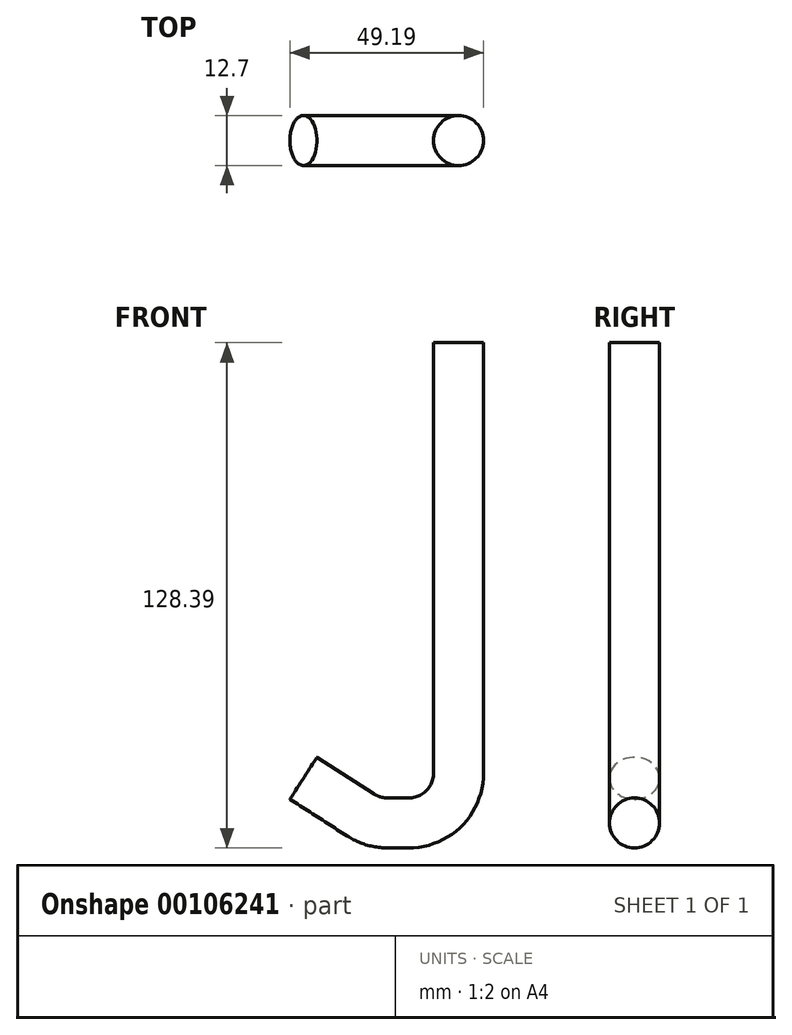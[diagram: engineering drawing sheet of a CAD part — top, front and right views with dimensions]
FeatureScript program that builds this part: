
annotation { "Feature Type Name" : "Feature", "Feature Type Description" : "" }
export const myFeature = defineFeature(function(context is Context, id is Id, definition is map)
    precondition{}
    {
        {
            var Q0;
            Q0=qCreatedBy(makeId("Front.planeOp"),FACE);
            var sketch = newSketch(context, id + "F0", { "sketchPlane" : qUnion([Q0])});
            skLineSegment(sketch, "E0", {"start": v(0, 63.86) * mm, "end": v(0, -45.48) * mm});
            skLineSegment(sketch, "E1", {"start": v(-12.7, -58.18) * mm, "end": v(-18, -58.18) * mm});
            skLineSegment(sketch, "E2", {"start": v(-24.86, -56.17) * mm, "end": v(-39.4, -46.83) * mm});
            skPoint(sketch, "E3.visualSharp", {"position": v(0, -58.18) * mm});
            skArc(sketch, "E3.filletArc", {"start": v(-12.7, -58.18) * mm, "mid": v(-3.72, -54.46) * mm, "end": v(0, -45.48) * mm});
            skPoint(sketch, "E4.visualSharp", {"position": v(-21.72, -58.18) * mm});
            skArc(sketch, "E4.filletArc", {"start": v(-24.86, -56.17) * mm, "mid": v(-21.57, -57.67) * mm, "end": v(-18, -58.18) * mm});
            skSolve(sketch);
        }
        {
            var Q0;
            Q0=sQuery(id+"F0.wireOp",VERTEX,"E0.start");
            var Q1;
            Q1=qCreatedBy(makeId("Top.planeOp"),FACE);
            cPlane(context, id + "F1", {"entities" : qUnion([Q0, Q1]), "cplaneType" : CPlaneType.PLANE_POINT, "offset" : 25.4 * mm, "width" : 152.4 * mm, "height" : 152.4 * mm});
        }
        {
            var Q0;
            Q0=qCreatedBy(id+"F1.planeOp",FACE);
            var sketch = newSketch(context, id + "F2", { "sketchPlane" : qUnion([Q0])});
            skCircle(sketch, "E5", {"center": v(0, 0) * mm, "radius": 6.35 * mm});
            skSolve(sketch);
        }
        {
            var Q0;
            Q0 = qSketchRegion(id + "F2", true);
            var Q1;
            Q1 = qConstructionFilter(qBodyType(qCreatedBy(id + "F0" ,EDGE), BodyType.WIRE), ConstructionObject.NO);
            sweep(context, id + "F3", {"profiles" : qUnion([Q0]), "path" : qUnion([Q1])});
        }
    });
